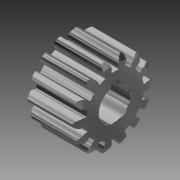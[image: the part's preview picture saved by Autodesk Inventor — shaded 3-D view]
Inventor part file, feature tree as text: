
AUTODESK INVENTOR PART (.ipt)
format: ipt  version: 2014 (Build 180170000, 170)  size: 321,024 bytes
history: native  units: mm (DEFAULTED — no unit token found)
features: extrude x2, chamfer x2, sketch x2, other x1
ambient origin geometry x8: Origin, YZ Plane, XZ Plane, XY Plane, X Axis, Y Axis, Z Axis, Center Point
bodies: Solid1 (feature_tree)
feature tree (7):
  other  "Gear Blank"
  extrude  "Tooth Profile"  Depth=17.213665mm
  chamfer  "Bore Chamfer Interior"  Distance=8.89mm
  chamfer  "Bore Chamfer Exterior"  Distance=140.0mm
  extrude  "Key"  Depth=2.0mm
  sketch  "Sketch2"  dims[d12=90.0deg d24=17.213665mm]
  sketch  "Sketch16"  dims[d26=0.0mm d77=8.89mm d83=140.0mm d95=0.127mm d96=3.175mm d97=0.127mm d98=3.175mm d104=10.16mm d108=30.0deg d109=30.0deg d110=12.7mm d112=0.254mm d117=2.0mm d118=3.0mm d119=25.4mm d120=0.0mm d121=45.0deg d122=45.0deg]
